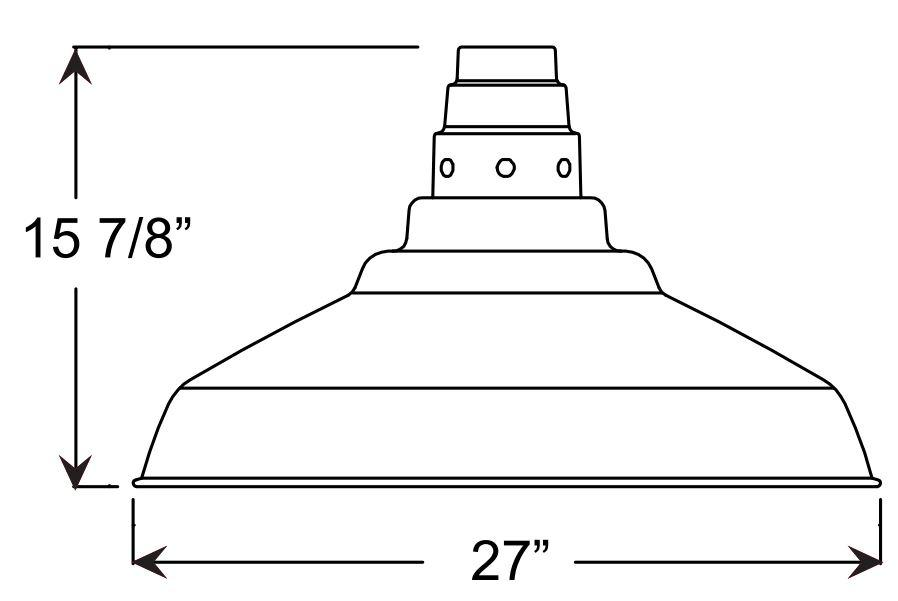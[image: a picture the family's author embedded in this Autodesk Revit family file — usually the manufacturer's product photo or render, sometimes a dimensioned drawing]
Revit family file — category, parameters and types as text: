
# Revit family: VEC 12,16,20,24 MB
name_source: partatom
category: Lighting Fixtures
units: mm (PartAtom-declared; Revit-internal decimal feet)

## family parameters
Always vertical = Yes
Cut with Voids When Loaded = No
Light Source = Yes
OmniClass Number = 23.80.70.00
OmniClass Title = Lighting
Part Type = Normal
Room Calculation Point = No
Round Connector Dimension = Use Diameter
Shared = No
Work Plane-Based = No

## types (4) — shared parameters
Apparent Load = 200 VA
Body Colour = Spun aluminium
Body Material = body
Bulb = Bulb
CRI = >90
Canopy Body = body
Color Filter = 16777215
Construction Material = Heavy Duty spun aluminum.
Default Elevation = 0' - 0"
Description = 120-277 Voltage
Dimming = 1%
Dimming Lamp Color Temperature Shift = <None>
Efficiency = 71-108 lumens per watt
HUB = Steel, Paint Finish, Dark Gray, Matte
Lamp = MB
Life = L70 50,000 hours
Load Classification = Lighting
Manufacturer = ANP Lighting
Power Factor = 1
Tilt Angle = 90.00°
URL = https://www.anplighting.com
Voltage = 220 V
Warranty = 5 year limited warranty
Wattage Comments = 200 W Max
b = 0' - 0"

## per-type parameters (varying)
| type | Fixture Diameter | Fixture Height | Photometric Web File | VEC12 | VEC16 | VEC20 | VEC24 | Weight | a |
| VEC12 | 1' - 0" | 0' - 6 1/4" | VEC12M016LDDW40K.ies | Yes | No | No | No | 1.5lbs | 0' - 6" |
| VEC16 | 1' - 4" | 0' - 8 1/2" | VEC16M016LDDW40K.ies | No | Yes | No | No | 2.5lbs | 0' - 6" |
| VEC20 | 1' - 8" | 0' - 10 1/2" | VEC20M016LDDW40K.ies | No | No | Yes | No | 4.0lbs | 0' - 7 1/2" |
| VEC24 | 2' - 0" | 1' - 0 3/4" | VEC24M016LDDW40K.ies | No | No | No | Yes | 5.0lb | 0' - 8 1/2" |

note: column(s) folded — value = type name in every type: Model

## geometry (parser evidence)
native form markers: Sweep x29
no freeform markers — native parametric forms only
